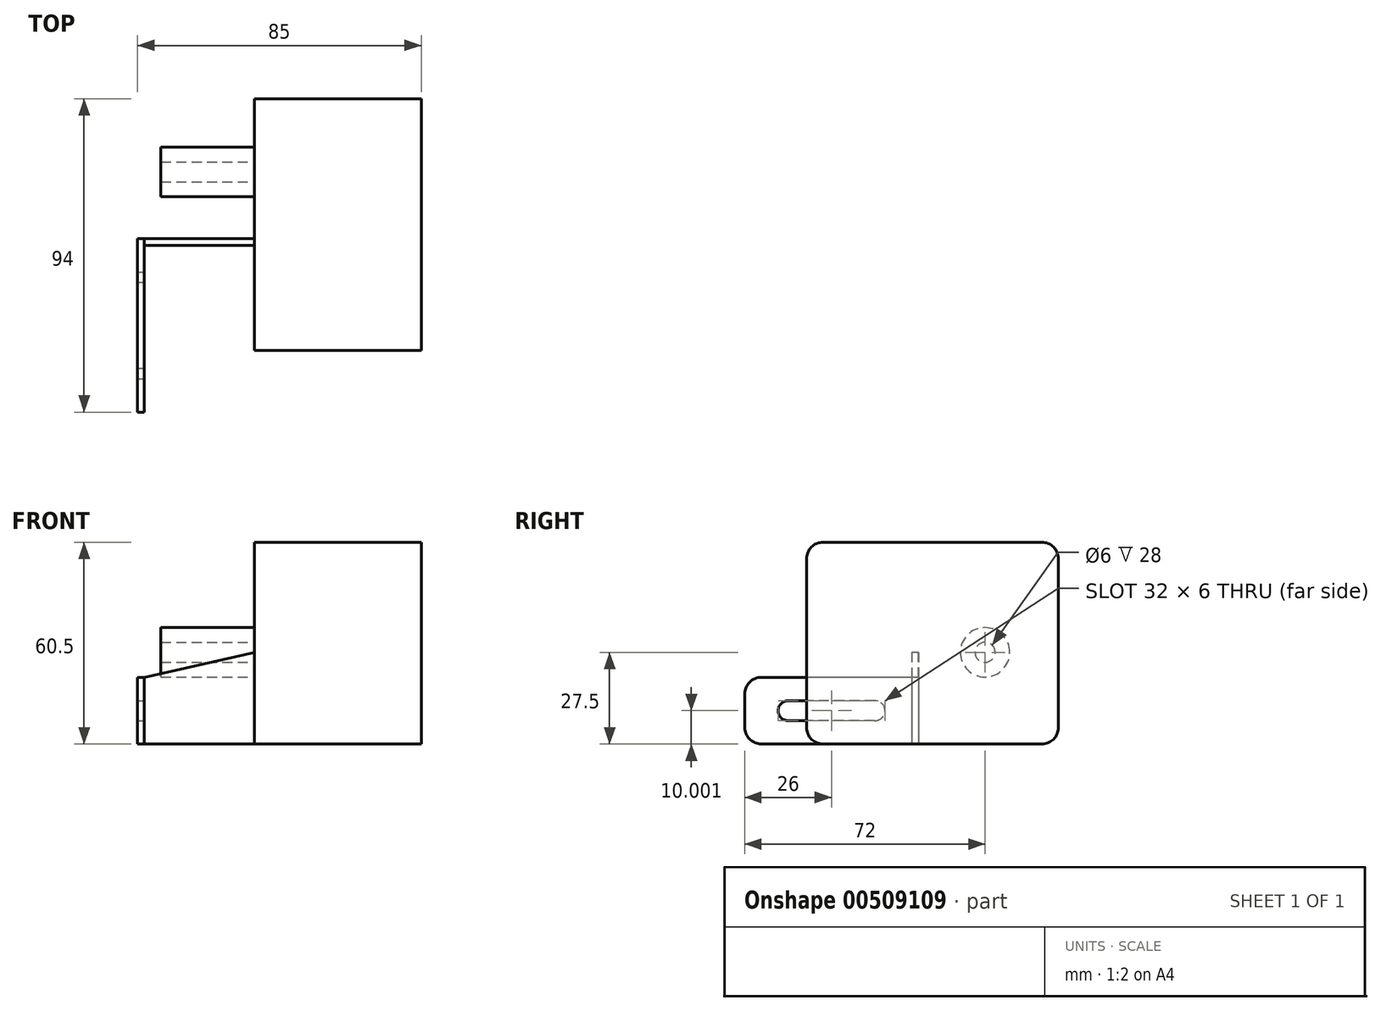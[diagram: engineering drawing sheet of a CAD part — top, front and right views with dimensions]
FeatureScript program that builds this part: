
annotation { "Feature Type Name" : "Feature", "Feature Type Description" : "" }
export const myFeature = defineFeature(function(context is Context, id is Id, definition is map)
    precondition{}
    {
        {
            var Q0;
            Q0=qCreatedBy(makeId("Right.planeOp"),FACE);
            var sketch = newSketch(context, id + "F0", { "sketchPlane" : qUnion([Q0])});
            skLineSegment(sketch, "E0.bottom", {"start": v(5, 0) * mm, "end": v(70.5, 0) * mm});
            skLineSegment(sketch, "E0.top", {"start": v(5, 60.5) * mm, "end": v(70.5, 60.5) * mm});
            skLineSegment(sketch, "E0.left", {"start": v(0, 5) * mm, "end": v(0, 55.5) * mm});
            skLineSegment(sketch, "E0.right", {"start": v(75.5, 5) * mm, "end": v(75.5, 55.5) * mm});
            skPoint(sketch, "E1.visualSharp", {"position": v(0, 60.5) * mm});
            skArc(sketch, "E1.filletArc", {"start": v(5, 60.5) * mm, "mid": v(1.46, 59.04) * mm, "end": v(0, 55.5) * mm});
            skPoint(sketch, "E2.visualSharp", {"position": v(0, 0) * mm});
            skArc(sketch, "E2.filletArc", {"start": v(0, 5) * mm, "mid": v(1.46, 1.46) * mm, "end": v(5, 0) * mm});
            skPoint(sketch, "E3.visualSharp", {"position": v(75.5, 0) * mm});
            skArc(sketch, "E3.filletArc", {"start": v(70.5, 0) * mm, "mid": v(74.04, 1.46) * mm, "end": v(75.5, 5) * mm});
            skPoint(sketch, "E4.visualSharp", {"position": v(75.5, 60.5) * mm});
            skArc(sketch, "E4.filletArc", {"start": v(75.5, 55.5) * mm, "mid": v(74.04, 59.04) * mm, "end": v(70.5, 60.5) * mm});
            skSolve(sketch);
        }
        {
            var Q0;
            Q0 = qSketchRegion(id + "F0", true);
            extrude(context, id + "F1", {"entities" : qUnion([Q0]), "depth" : 50 * mm, "offsetDistance" : 25 * mm});
        }
        {
            var Q0;
            Q0=makeQuery(id+"F1.opExtrude","CAP_FACE",FACE,{"disambiguationData":[OSD([sQuery(id+"F0.wireOp",EDGE,"E0.bottom"),sQuery(id+"F0.wireOp",EDGE,"E0.top"),sQuery(id+"F0.wireOp",EDGE,"E0.left"),sQuery(id+"F0.wireOp",EDGE,"E0.right"),sQuery(id+"F0.wireOp",EDGE,"E1.filletArc"),sQuery(id+"F0.wireOp",EDGE,"E2.filletArc"),sQuery(id+"F0.wireOp",EDGE,"E3.filletArc"),sQuery(id+"F0.wireOp",EDGE,"E4.filletArc")])],"isStart":true});
            var sketch = newSketch(context, id + "F2", { "sketchPlane" : qUnion([Q0])});
            skCircle(sketch, "E5", {"center": v(-53.5, 27.5) * mm, "radius": 7.4 * mm});
            skCircle(sketch, "E6", {"center": v(-53.5, 27.5) * mm, "radius": 3 * mm});
            skSolve(sketch);
        }
        {
            var Q0;
            Q0 = qSketchRegion(id + "F2", true);
            extrude(context, id + "F3", {"entities" : qUnion([Q0]), "operationType" : NewBodyOperationType.ADD, "depth" : 28 * mm, "offsetDistance" : 25 * mm});
        }
        {
            var Q0;
            {var subQ0=sQuery(id+"F0.wireOp",EDGE,"E0.left");var subQ1=sQuery(id+"F0.wireOp",EDGE,"E0.top");var subQ2=sQuery(id+"F0.wireOp",EDGE,"E0.right");var subQ3=sQuery(id+"F0.wireOp",EDGE,"E0.bottom");var subQ4=sQuery(id+"F0.wireOp",EDGE,"E1.filletArc");var subQ5=sQuery(id+"F0.wireOp",EDGE,"E2.filletArc");var subQ6=sQuery(id+"F0.wireOp",EDGE,"E3.filletArc");var subQ7=sQuery(id+"F0.wireOp",EDGE,"E4.filletArc");Q0=makeQuery(id+"F3.boolean.opBoolean","SPLIT",FACE,{"disambiguationData":[TD([makeQuery(id+"F1.opExtrude","SWEPT_FACE",FACE,{"disambiguationData":[OSD([subQ3])]})])],"derivedFrom":makeQuery(id+"F1.opExtrude","CAP_FACE",FACE,{"disambiguationData":[OSD([subQ3,subQ1,subQ0,subQ2,subQ4,subQ5,subQ6,subQ7])],"isStart":true})});}
            var sketch = newSketch(context, id + "F4", { "sketchPlane" : qUnion([Q0])});
            skLineSegment(sketch, "E7", {"start": v(-53.5, 27.5) * mm, "end": v(-33.5, 27.5) * mm, "construction": true});
            skLineSegment(sketch, "E8.bottom", {"start": v(-33.5, 27.5) * mm, "end": v(-31.5, 27.5) * mm});
            skLineSegment(sketch, "E8.top", {"start": v(-33.5, 0) * mm, "end": v(-31.5, 0) * mm});
            skLineSegment(sketch, "E8.left", {"start": v(-33.5, 27.5) * mm, "end": v(-33.5, 0) * mm});
            skLineSegment(sketch, "E8.right", {"start": v(-31.5, 27.5) * mm, "end": v(-31.5, 0) * mm});
            skSolve(sketch);
        }
        {
            var Q0;
            Q0 = qSketchRegion(id + "F4", true);
            extrude(context, id + "F5", {"entities" : qUnion([Q0]), "operationType" : NewBodyOperationType.ADD, "depth" : 33 * mm, "offsetDistance" : 25 * mm});
        }
        {
            var Q0;
            Q0=makeQuery(id+"F5.opExtrude","CAP_FACE",FACE,{"disambiguationData":[OSD([sQuery(id+"F4.wireOp",EDGE,"E8.bottom"),sQuery(id+"F4.wireOp",EDGE,"E8.top"),sQuery(id+"F4.wireOp",EDGE,"E8.left"),sQuery(id+"F4.wireOp",EDGE,"E8.right")])],"isStart":false});
            var sketch = newSketch(context, id + "F6", { "sketchPlane" : qUnion([Q0])});
            skLineSegment(sketch, "E9.bottom", {"start": v(-33.5, 0) * mm, "end": v(13.5, 0) * mm});
            skLineSegment(sketch, "E9.top", {"start": v(-33.5, 20) * mm, "end": v(13.5, 20) * mm});
            skLineSegment(sketch, "E9.left", {"start": v(-33.5, 0) * mm, "end": v(-33.5, 20) * mm});
            skLineSegment(sketch, "E9.right", {"start": v(18.5, 5) * mm, "end": v(18.5, 15) * mm});
            skLineSegment(sketch, "E10", {"start": v(18.5, 10) * mm, "end": v(5.5, 10) * mm, "construction": true});
            skArc(sketch, "E11", {"start": v(5.39, 7) * mm, "mid": v(8.5, 9.94) * mm, "end": v(5.5, 13) * mm});
            skLineSegment(sketch, "E12", {"start": v(5.5, 10) * mm, "end": v(-20.5, 10) * mm, "construction": true});
            skArc(sketch, "E13", {"start": v(-20.5, 13) * mm, "mid": v(-23.5, 9.95) * mm, "end": v(-20.39, 7) * mm});
            skLineSegment(sketch, "E14", {"start": v(-20.5, 13) * mm, "end": v(5.5, 13) * mm});
            skLineSegment(sketch, "E15", {"start": v(-20.39, 7) * mm, "end": v(5.61, 7) * mm});
            skPoint(sketch, "E16.visualSharp", {"position": v(18.5, 20) * mm});
            skArc(sketch, "E16.filletArc", {"start": v(18.5, 15) * mm, "mid": v(17.04, 18.54) * mm, "end": v(13.5, 20) * mm});
            skPoint(sketch, "E17.visualSharp", {"position": v(18.5, 0) * mm});
            skArc(sketch, "E17.filletArc", {"start": v(13.5, 0) * mm, "mid": v(17.04, 1.46) * mm, "end": v(18.5, 5) * mm});
            skSolve(sketch);
        }
        {
            var Q0;
            Q0 = qSketchRegion(id + "F6", true);
            extrude(context, id + "F7", {"entities" : qUnion([Q0]), "operationType" : NewBodyOperationType.ADD, "depth" : 2 * mm, "offsetDistance" : 25 * mm});
        }
        {
            var Q0;
            Q0=makeQuery(id+"F7.boolean.opBoolean","MERGE",FACE,{"derivedFrom":[makeQuery(id+"F5.opExtrude","SWEPT_FACE",FACE,{"disambiguationData":[OSD([sQuery(id+"F4.wireOp",EDGE,"E8.left")])]}),makeQuery(id+"F7.opExtrude","SWEPT_FACE",FACE,{"disambiguationData":[OSD([sQuery(id+"F6.wireOp",EDGE,"E9.left")])]})]});
            var sketch = newSketch(context, id + "F8", { "sketchPlane" : qUnion([Q0])});
            skLineSegment(sketch, "E18", {"start": v(33, 20) * mm, "end": v(0, 27.5) * mm});
            skLineSegment(sketch, "E19", {"start": v(0, 27.5) * mm, "end": v(19.24, 38.77) * mm});
            skLineSegment(sketch, "E20", {"start": v(19.24, 38.77) * mm, "end": v(42.12, 30.8) * mm});
            skLineSegment(sketch, "E21", {"start": v(42.12, 30.8) * mm, "end": v(33, 20) * mm});
            skSolve(sketch);
        }
        {
            var Q0;
            Q0 = qSketchRegion(id + "F8", true);
            extrude(context, id + "F9", {"entities" : qUnion([Q0]), "operationType" : NewBodyOperationType.REMOVE, "oppositeDirection" : true, "depth" : 25 * mm, "offsetDistance" : 25 * mm});
        }
    });
